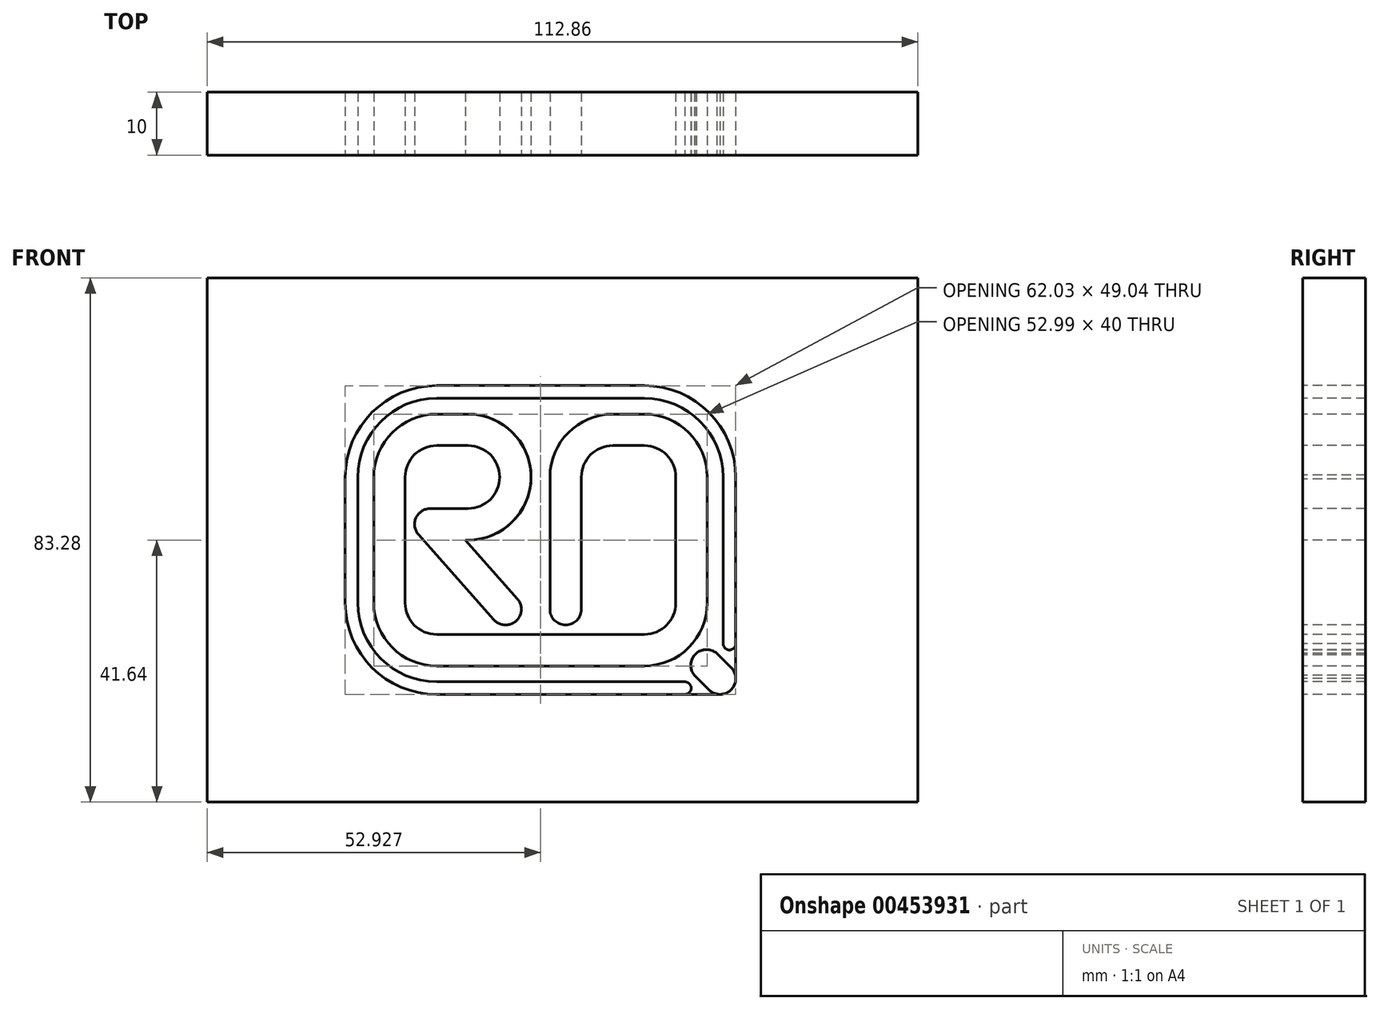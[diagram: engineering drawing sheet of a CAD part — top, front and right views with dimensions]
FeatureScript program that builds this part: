
annotation { "Feature Type Name" : "Feature", "Feature Type Description" : "" }
export const myFeature = defineFeature(function(context is Context, id is Id, definition is map)
    precondition{}
    {
        {
            var Q0;
            Q0=qCreatedBy(makeId("Front.planeOp"),FACE);
            var sketch = newSketch(context, id + "F0", { "sketchPlane" : qUnion([Q0])});
            skPoint(sketch, "E0.middle", {"position": v(0, 0) * mm});
            skLineSegment(sketch, "E1", {"start": v(-25, 10) * mm, "end": v(-25, -10) * mm});
            skLineSegment(sketch, "E2", {"start": v(-2, -20) * mm, "end": v(-0.38, -20) * mm});
            skLineSegment(sketch, "E3", {"start": v(-2, -11) * mm, "end": v(-2, 10) * mm});
            skLineSegment(sketch, "E4", {"start": v(8, 20) * mm, "end": v(13, 20) * mm});
            skLineSegment(sketch, "E5", {"start": v(23, 10) * mm, "end": v(23, -10) * mm});
            skLineSegment(sketch, "E6", {"start": v(13, -20) * mm, "end": v(9, -20) * mm});
            skLineSegment(sketch, "E7", {"start": v(-25, 20) * mm, "end": v(-15, 20) * mm});
            skLineSegment(sketch, "E8", {"start": v(-21, 0) * mm, "end": v(-15, 0) * mm});
            skLineSegment(sketch, "E9", {"start": v(-5, 10.33) * mm, "end": v(-5, 10.33) * mm});
            skPoint(sketch, "E10.visualSharp", {"position": v(-5.33, 20) * mm});
            skArc(sketch, "E10.filletArc", {"start": v(-5, 10.33) * mm, "mid": v(-8.05, 17.19) * mm, "end": v(-15, 20) * mm});
            skArc(sketch, "E11.filletArc", {"start": v(-15, 0) * mm, "mid": v(-7.81, 3.05) * mm, "end": v(-5, 10.33) * mm});
            skPoint(sketch, "E12.visualSharp", {"position": v(-3.63, -20) * mm});
            skPoint(sketch, "E13.visualSharp", {"position": v(23, -20) * mm});
            skArc(sketch, "E13.filletArc", {"start": v(13, -20) * mm, "mid": v(20.07, -17.07) * mm, "end": v(23, -10) * mm});
            skPoint(sketch, "E14.visualSharp", {"position": v(23, 20) * mm});
            skArc(sketch, "E14.filletArc", {"start": v(23, 10) * mm, "mid": v(20.07, 17.07) * mm, "end": v(13, 20) * mm});
            skPoint(sketch, "E15.visualSharp", {"position": v(-2, 20) * mm});
            skArc(sketch, "E15.filletArc", {"start": v(8, 20) * mm, "mid": v(0.92, 17.07) * mm, "end": v(-2, 10) * mm});
            skPoint(sketch, "E16.visualSharp", {"position": v(-2, -20) * mm});
            skArc(sketch, "E17.0", {"start": v(8, 15) * mm, "mid": v(4.46, 13.54) * mm, "end": v(3, 10) * mm});
            skLineSegment(sketch, "E17.1", {"start": v(3, -11) * mm, "end": v(3, 10) * mm});
            skLineSegment(sketch, "E17.2", {"start": v(8, 15) * mm, "end": v(13, 15) * mm});
            skArc(sketch, "E17.4", {"start": v(18, 10) * mm, "mid": v(16.53, 13.54) * mm, "end": v(13, 15) * mm});
            skLineSegment(sketch, "E17.5", {"start": v(18, 10) * mm, "end": v(18, -10) * mm});
            skArc(sketch, "E17.6", {"start": v(13, -15) * mm, "mid": v(16.53, -13.54) * mm, "end": v(18, -10) * mm});
            skLineSegment(sketch, "E17.7", {"start": v(13, -15) * mm, "end": v(9, -15) * mm});
            skArc(sketch, "E18.1", {"start": v(-15, 5) * mm, "mid": v(-11.44, 6.5) * mm, "end": v(-10, 10.08) * mm});
            skArc(sketch, "E18.2", {"start": v(-10, 10.08) * mm, "mid": v(-11.5, 13.56) * mm, "end": v(-15, 15) * mm});
            skLineSegment(sketch, "E18.3", {"start": v(-20, 15) * mm, "end": v(-15, 15) * mm});
            skLineSegment(sketch, "E19.0", {"start": v(-30, 17.5) * mm, "end": v(-30, -10) * mm});
            skLineSegment(sketch, "E20.0", {"start": v(-1, -15) * mm, "end": v(-0.38, -15) * mm});
            skLineSegment(sketch, "E21", {"start": v(-20, -20) * mm, "end": v(-2, -20) * mm});
            skLineSegment(sketch, "E22", {"start": v(-1, -15) * mm, "end": v(9, -15) * mm});
            skLineSegment(sketch, "E23.0", {"start": v(-20, -15) * mm, "end": v(0, -15) * mm});
            skLineSegment(sketch, "E24", {"start": v(-5, 10.33) * mm, "end": v(-5, 0) * mm});
            skLineSegment(sketch, "E25", {"start": v(0.5, -13.5) * mm, "end": v(0.5, -13.5) * mm});
            skPoint(sketch, "E26.visualSharp", {"position": v(3, -13.5) * mm});
            skArc(sketch, "E26.filletArc", {"start": v(0.5, -13.5) * mm, "mid": v(2.26, -12.77) * mm, "end": v(3, -11) * mm});
            skPoint(sketch, "E27.newPointB", {"position": v(-23.5, -13.5) * mm});
            skArc(sketch, "E27.filletArc", {"start": v(-2, -11) * mm, "mid": v(-1.27, -12.77) * mm, "end": v(0.5, -13.5) * mm});
            skPoint(sketch, "E28.visualSharp", {"position": v(-30, -20) * mm});
            skArc(sketch, "E28.filletArc", {"start": v(-30, -19.5) * mm, "mid": v(-29.85, -19.85) * mm, "end": v(-29.5, -20) * mm});
            skLineSegment(sketch, "E29", {"start": v(-7.28, -12.77) * mm, "end": v(-7.28, -12.77) * mm});
            skArc(sketch, "E30.filletArc", {"start": v(-7.28, -12.77) * mm, "mid": v(-6.55, -11) * mm, "end": v(-7.27, -9.24) * mm});
            skArc(sketch, "E31.filletArc", {"start": v(-11.23, -12.21) * mm, "mid": v(-9.4, -13.48) * mm, "end": v(-7.28, -12.77) * mm});
            skLineSegment(sketch, "E32.0", {"start": v(19.16, -19.7) * mm, "end": v(23.25, -23.79) * mm});
            skLineSegment(sketch, "E33.0", {"start": v(14.76, -15.3) * mm, "end": v(14.29, -14.83) * mm});
            skPoint(sketch, "E34.newPointB", {"position": v(-25, 20) * mm});
            skPoint(sketch, "E35.visualSharp", {"position": v(-23.5, 5) * mm});
            skPoint(sketch, "E36.visualSharp", {"position": v(-23.5, 0) * mm});
            skLineSegment(sketch, "E37", {"start": v(-30, 10) * mm, "end": v(-30, 17.5) * mm});
            skLineSegment(sketch, "E38", {"start": v(-20, 20) * mm, "end": v(-25, 20) * mm});
            skPoint(sketch, "E39.visualSharp", {"position": v(-30, 20) * mm});
            skArc(sketch, "E39.filletArc", {"start": v(-20, 20) * mm, "mid": v(-27.07, 17.07) * mm, "end": v(-30, 10) * mm});
            skArc(sketch, "E40", {"start": v(23.25, -23.79) * mm, "mid": v(26.79, -23.79) * mm, "end": v(26.78, -20.25) * mm});
            skPoint(sketch, "E41", {"position": v(20.07, -17.07) * mm});
            skPoint(sketch, "E42.orphan", {"position": v(16.53, -13.54) * mm});
            skLineSegment(sketch, "E43.trimOffspring", {"start": v(13, -20) * mm, "end": v(-0.38, -20) * mm});
            skArc(sketch, "E44.trimOffspring", {"start": v(19.16, -19.7) * mm, "mid": v(21.12, -18.14) * mm, "end": v(22.69, -16.19) * mm});
            skPoint(sketch, "E45.newPointB", {"position": v(-25, -20) * mm});
            skArc(sketch, "E45.filletArc", {"start": v(-25, -10) * mm, "mid": v(-23.54, -13.54) * mm, "end": v(-20, -15) * mm});
            skLineSegment(sketch, "E46", {"start": v(-15, 20) * mm, "end": v(8, 20) * mm});
            skLineSegment(sketch, "E47", {"start": v(21.86, -24.52) * mm, "end": v(-20, -24.52) * mm});
            skLineSegment(sketch, "E48", {"start": v(27.51, -22.02) * mm, "end": v(27.51, -18.87) * mm});
            skLineSegment(sketch, "E49", {"start": v(13, 24.52) * mm, "end": v(-20, 24.52) * mm});
            skLineSegment(sketch, "E50", {"start": v(-34.52, -10) * mm, "end": v(-34.52, 10) * mm});
            skPoint(sketch, "E51.orphan", {"position": v(17.43, -17.97) * mm});
            skPoint(sketch, "E52.orphan", {"position": v(13.35, -13.89) * mm});
            skArc(sketch, "E53.0", {"start": v(27.51, 10) * mm, "mid": v(23.26, 20.27) * mm, "end": v(13, 24.52) * mm});
            skArc(sketch, "E54.0", {"start": v(25.51, 10) * mm, "mid": v(21.85, 18.85) * mm, "end": v(13, 22.52) * mm});
            skLineSegment(sketch, "E55.0", {"start": v(25.51, -22.07) * mm, "end": v(25.51, -19) * mm});
            skLineSegment(sketch, "E56.0", {"start": v(25.02, -22.52) * mm, "end": v(21.98, -22.52) * mm});
            skLineSegment(sketch, "E57.0", {"start": v(-32.52, -10) * mm, "end": v(-32.52, 10) * mm});
            skLineSegment(sketch, "E58.0", {"start": v(13, 22.52) * mm, "end": v(-20, 22.52) * mm});
            skPoint(sketch, "E59.visualSharp", {"position": v(-32.52, 22.52) * mm});
            skArc(sketch, "E59.filletArc", {"start": v(-20, 22.52) * mm, "mid": v(-28.85, 18.85) * mm, "end": v(-32.52, 10) * mm});
            skArc(sketch, "E60.0", {"start": v(-20, 24.52) * mm, "mid": v(-30.27, 20.27) * mm, "end": v(-34.52, 10) * mm});
            skPoint(sketch, "E61.visualSharp", {"position": v(-32.52, -22.52) * mm});
            skLineSegment(sketch, "E62", {"start": v(26.51, -15) * mm, "end": v(26.51, -16.32) * mm});
            skLineSegment(sketch, "E63.0", {"start": v(18.1, -20.77) * mm, "end": v(22.19, -24.85) * mm, "construction": true});
            skLineSegment(sketch, "E64.0", {"start": v(23.75, -15.12) * mm, "end": v(27.84, -19.2) * mm, "construction": true});
            skArc(sketch, "E65", {"start": v(19.44, -24.52) * mm, "mid": v(20.44, -23.52) * mm, "end": v(19.44, -22.52) * mm});
            skArc(sketch, "E66", {"start": v(25.51, -16.47) * mm, "mid": v(26.51, -17.47) * mm, "end": v(27.51, -16.47) * mm});
            skLineSegment(sketch, "E67.trimOffspring", {"start": v(25.51, -14) * mm, "end": v(25.51, 10) * mm});
            skLineSegment(sketch, "E68.trimOffspring", {"start": v(27.51, -14) * mm, "end": v(27.51, 33) * mm});
            skLineSegment(sketch, "E69.trimOffspring", {"start": v(19.86, -22.52) * mm, "end": v(-20, -22.52) * mm});
            skLineSegment(sketch, "E70", {"start": v(21.86, -24.52) * mm, "end": v(25.02, -24.52) * mm});
            skLineSegment(sketch, "E71", {"start": v(27.51, -14) * mm, "end": v(27.51, -22.02) * mm});
            skLineSegment(sketch, "E72.bottom", {"start": v(-56.43, 41.64) * mm, "end": v(56.43, 41.64) * mm});
            skLineSegment(sketch, "E72.top", {"start": v(-56.43, -41.64) * mm, "end": v(56.43, -41.64) * mm});
            skLineSegment(sketch, "E72.left", {"start": v(-56.43, 41.64) * mm, "end": v(-56.43, -41.64) * mm});
            skLineSegment(sketch, "E72.right", {"start": v(56.43, 41.64) * mm, "end": v(56.43, -41.64) * mm});
            skLineSegment(sketch, "E73", {"start": v(0, 0) * mm, "end": v(0, -38.7) * mm, "construction": true});
            skLineSegment(sketch, "E74", {"start": v(0, 0) * mm, "end": v(33.56, 0) * mm, "construction": true});
            skArc(sketch, "E75.filletArc", {"start": v(-20, 15) * mm, "mid": v(-23.54, 13.54) * mm, "end": v(-25, 10) * mm});
            skArc(sketch, "E76.0", {"start": v(-30, -10) * mm, "mid": v(-27.07, -17.07) * mm, "end": v(-20, -20) * mm});
            skArc(sketch, "E77.0", {"start": v(-34.52, -10) * mm, "mid": v(-30.27, -20.27) * mm, "end": v(-20, -24.52) * mm});
            skArc(sketch, "E78.0", {"start": v(-32.52, -10) * mm, "mid": v(-28.85, -18.85) * mm, "end": v(-20, -22.52) * mm});
            skLineSegment(sketch, "E79", {"start": v(-15, 5) * mm, "end": v(-21, 5) * mm});
            skLineSegment(sketch, "E80", {"start": v(-23.5, 2.5) * mm, "end": v(-23.5, 2.5) * mm});
            skArc(sketch, "E81.filletArc", {"start": v(-21, 5) * mm, "mid": v(-22.77, 4.27) * mm, "end": v(-23.5, 2.5) * mm});
            skArc(sketch, "E82.filletArc", {"start": v(-23.5, 2.5) * mm, "mid": v(-22.77, 0.73) * mm, "end": v(-21, 0) * mm});
            skLineSegment(sketch, "E83", {"start": v(-11.23, -12.21) * mm, "end": v(-18, 0) * mm, "construction": true});
            skPoint(sketch, "E84.startSnap0", {"position": v(-6.55, -11) * mm});
            skLineSegment(sketch, "E85.0", {"start": v(-6.86, -9.79) * mm, "end": v(-13.63, 2.42) * mm, "construction": true});
            skLineSegment(sketch, "E86", {"start": v(-22.87, 0.84) * mm, "end": v(-10.92, -12.66) * mm});
            skLineSegment(sketch, "E87.0", {"start": v(-19.13, 4.16) * mm, "end": v(-7.17, -9.34) * mm});
            skArc(sketch, "E88.0", {"start": v(13, -22.52) * mm, "mid": v(21.85, -18.85) * mm, "end": v(25.51, -10) * mm});
            skArc(sketch, "E89", {"start": v(24.48, -17.98) * mm, "mid": v(21.11, -18.13) * mm, "end": v(20.96, -21.5) * mm});
            skLineSegment(sketch, "E90", {"start": v(24.48, -17.98) * mm, "end": v(26.78, -20.25) * mm});
            skLineSegment(sketch, "E91", {"start": v(25.51, -16.47) * mm, "end": v(25.51, -14) * mm});
            skSolve(sketch);
        }
        {
            var Q0;
            Q0=makeQuery(id+"F0.imprint","IMPRINT",FACE,{"disambiguationData":[TD([[makeQuery(id+"F0.imprint","IMPRINT",EDGE,{"derivedFrom":sQuery(id+"F0.wireOp",EDGE,"E1")}),-1.0]])]});
            var Q1;
            {var subQ6=sQuery(id+"F0.wireOp",EDGE,"8dgEX87s-OnN3-UPAw-RyUf-tcfM0RuKeMZf");Q1=makeQuery(id+"F0.imprint","IMPRINT",FACE,{"disambiguationData":[TD([[makeQuery(id+"F0.imprint","IMPRINT",EDGE,{"derivedFrom":subQ6}),1.0]])]});}
            var Q2;
            {var subQ0=sQuery(id+"F0.wireOp",EDGE,"E40");var subQ1=makeQuery(id+"F0.imprint","INTERSECT",VERTEX,{"derivedFrom":[sQuery(id+"F0.wireOp",EDGE,"c0c087a9-fd36-4214-a694-875f0f01d769.0"),subQ0]});Q2=makeQuery(id+"F0.imprint","IMPRINT",FACE,{"disambiguationData":[TD([[makeQuery(id+"F0.imprint","IMPRINT",EDGE,{"disambiguationData":[TD([[subQ1,-1.0]])],"derivedFrom":subQ0}),1.0]])]});}
            var Q3;
            {var subQ0=sQuery(id+"F0.wireOp",EDGE,"E0.bottom");Q3=makeQuery(id+"F0.imprint","IMPRINT",FACE,{"disambiguationData":[TD([[makeQuery(id+"F0.imprint","IMPRINT",EDGE,{"derivedFrom":subQ0}),-1.0]])]});}
            var Q4;
            {var subQ0=sQuery(id+"F0.wireOp",EDGE,"E0.bottom");Q4=makeQuery(id+"F0.imprint","IMPRINT",FACE,{"disambiguationData":[TD([[makeQuery(id+"F0.imprint","IMPRINT",EDGE,{"derivedFrom":subQ0}),1.0]])]});}
            var Q5;
            {var subQ0=sQuery(id+"F0.wireOp",EDGE,"E31.filletArc");Q5=makeQuery(id+"F0.imprint","IMPRINT",FACE,{"disambiguationData":[TD([[makeQuery(id+"F0.imprint","IMPRINT",EDGE,{"derivedFrom":subQ0}),1.0]])]});}
            var Q6;
            {var subQ0=sQuery(id+"F0.wireOp",EDGE,"E89");var subQ1=sQuery(id+"F0.wireOp",EDGE,"E44.trimOffspring");var subQ2=makeQuery(id+"F0.imprint","INTERSECT",VERTEX,{"disambiguationData":[OD(0.0)],"derivedFrom":[subQ1,subQ0]});Q6=makeQuery(id+"F0.imprint","IMPRINT",FACE,{"disambiguationData":[TD([[makeQuery(id+"F0.imprint","IMPRINT",EDGE,{"disambiguationData":[TD([[subQ2,-1.0]])],"derivedFrom":subQ1}),-1.0]])]});}
            var Q7;
            {var subQ6=sQuery(id+"F0.wireOp",EDGE,"E32.0");var subQ8=makeQuery(id+"F0.imprint","IMPRINT",VERTEX,{"derivedFrom":subQ6});Q7=makeQuery(id+"F0.imprint","IMPRINT",FACE,{"disambiguationData":[TD([[makeQuery(id+"F0.imprint","IMPRINT",EDGE,{"disambiguationData":[TD([[subQ8,1.0]])],"derivedFrom":subQ6}),1.0]])]});}
            var Q8;
            {var subQ0=sQuery(id+"F0.wireOp",EDGE,"E89");var subQ1=sQuery(id+"F0.wireOp",EDGE,"E44.trimOffspring");var subQ2=makeQuery(id+"F0.imprint","INTERSECT",VERTEX,{"disambiguationData":[OD(0.0)],"derivedFrom":[subQ1,subQ0]});Q8=makeQuery(id+"F0.imprint","IMPRINT",FACE,{"disambiguationData":[TD([[makeQuery(id+"F0.imprint","IMPRINT",EDGE,{"disambiguationData":[TD([[subQ2,1.0]])],"derivedFrom":subQ1}),-1.0]])]});}
            extrude(context, id + "F1", {"entities" : qUnion([Q0, Q1, Q2, Q3, Q4, Q5, Q6, Q7, Q8]), "oppositeDirection" : true, "depth" : 10 * mm});
        }
        {
            var Q0;
            Q0=makeQuery(id+"F0.imprint","IMPRINT",FACE,{"disambiguationData":[TD([[makeQuery(id+"F0.imprint","IMPRINT",EDGE,{"derivedFrom":sQuery(id+"F0.wireOp",EDGE,"E1")}),1.0]])]});
            var Q1;
            {var subQ16=sQuery(id+"F0.wireOp",EDGE,"E2");Q1=makeQuery(id+"F0.imprint","IMPRINT",FACE,{"disambiguationData":[TD([[makeQuery(id+"F0.imprint","IMPRINT",EDGE,{"derivedFrom":subQ16}),-1.0]])]});}
            var Q2;
            {var subQ10=sQuery(id+"F0.wireOp",EDGE,"E65");Q2=makeQuery(id+"F0.imprint","IMPRINT",FACE,{"disambiguationData":[TD([[makeQuery(id+"F0.imprint","IMPRINT",EDGE,{"derivedFrom":subQ10}),-1.0]])]});}
            var Q3;
            {var subQ0=sQuery(id+"F0.wireOp",EDGE,"E44.trimOffspring");var subQ1=sQuery(id+"F0.wireOp",EDGE,"E32.0");var subQ2=makeQuery(id+"F0.imprint","INTERSECT",VERTEX,{"derivedFrom":[subQ1,subQ0]});Q3=makeQuery(id+"F0.imprint","IMPRINT",FACE,{"disambiguationData":[TD([[makeQuery(id+"F0.imprint","IMPRINT",EDGE,{"disambiguationData":[TD([[subQ2,-1.0]])],"derivedFrom":subQ1}),1.0]])]});}
            var Q4;
            {var subQ0=sQuery(id+"F0.wireOp",EDGE,"E89");var subQ1=sQuery(id+"F0.wireOp",EDGE,"E32.0");var subQ2=makeQuery(id+"F0.imprint","INTERSECT",VERTEX,{"derivedFrom":[subQ1,subQ0]});Q4=makeQuery(id+"F0.imprint","IMPRINT",FACE,{"disambiguationData":[TD([[makeQuery(id+"F0.imprint","IMPRINT",EDGE,{"disambiguationData":[TD([[subQ2,1.0]])],"derivedFrom":subQ1}),1.0]])]});}
            var Q5;
            {var subQ1=sQuery(id+"F0.wireOp",EDGE,"E66");Q5=makeQuery(id+"F0.imprint","IMPRINT",FACE,{"disambiguationData":[TD([[makeQuery(id+"F0.imprint","IMPRINT",EDGE,{"derivedFrom":subQ1}),-1.0]])]});}
            extrude(context, id + "F2", {"entities" : qUnion([Q0, Q1, Q2, Q3, Q4, Q5]), "oppositeDirection" : true, "depth" : 10 * mm});
        }
        {
            var Q0;
            Q0=makeQuery(id+"F0.imprint","IMPRINT",FACE,{"disambiguationData":[TD([[makeQuery(id+"F0.imprint","IMPRINT",EDGE,{"derivedFrom":sQuery(id+"F0.wireOp",EDGE,"E49")}),1.0]])]});
            var Q1;
            {var subQ0=sQuery(id+"F0.wireOp",EDGE,"E65");var subQ2=makeQuery(id+"F0.imprint","IMPRINT",VERTEX,{"derivedFrom":subQ0});Q1=makeQuery(id+"F0.imprint","IMPRINT",FACE,{"disambiguationData":[TD([[makeQuery(id+"F0.imprint","IMPRINT",EDGE,{"disambiguationData":[TD([[subQ2,-1.0]])],"derivedFrom":subQ0}),1.0]])]});}
            var Q2;
            {var subQ0=sQuery(id+"F0.wireOp",EDGE,"E66");var subQ3=makeQuery(id+"F0.imprint","IMPRINT",VERTEX,{"derivedFrom":subQ0});Q2=makeQuery(id+"F0.imprint","IMPRINT",FACE,{"disambiguationData":[TD([[makeQuery(id+"F0.imprint","IMPRINT",EDGE,{"disambiguationData":[TD([[subQ3,1.0]])],"derivedFrom":subQ0}),1.0]])]});}
            extrude(context, id + "F3", {"entities" : qUnion([Q0, Q1, Q2]), "oppositeDirection" : true, "depth" : 10 * mm});
        }
        {
            var Q0;
            Q0=makeQuery(id+"F0.imprint","IMPRINT",FACE,{"disambiguationData":[TD([[makeQuery(id+"F0.imprint","IMPRINT",EDGE,{"derivedFrom":sQuery(id+"F0.wireOp",EDGE,"E49")}),-1.0]])]});
            extrude(context, id + "F4", {"entities" : qUnion([Q0]), "oppositeDirection" : true, "depth" : 10 * mm});
        }
    });
